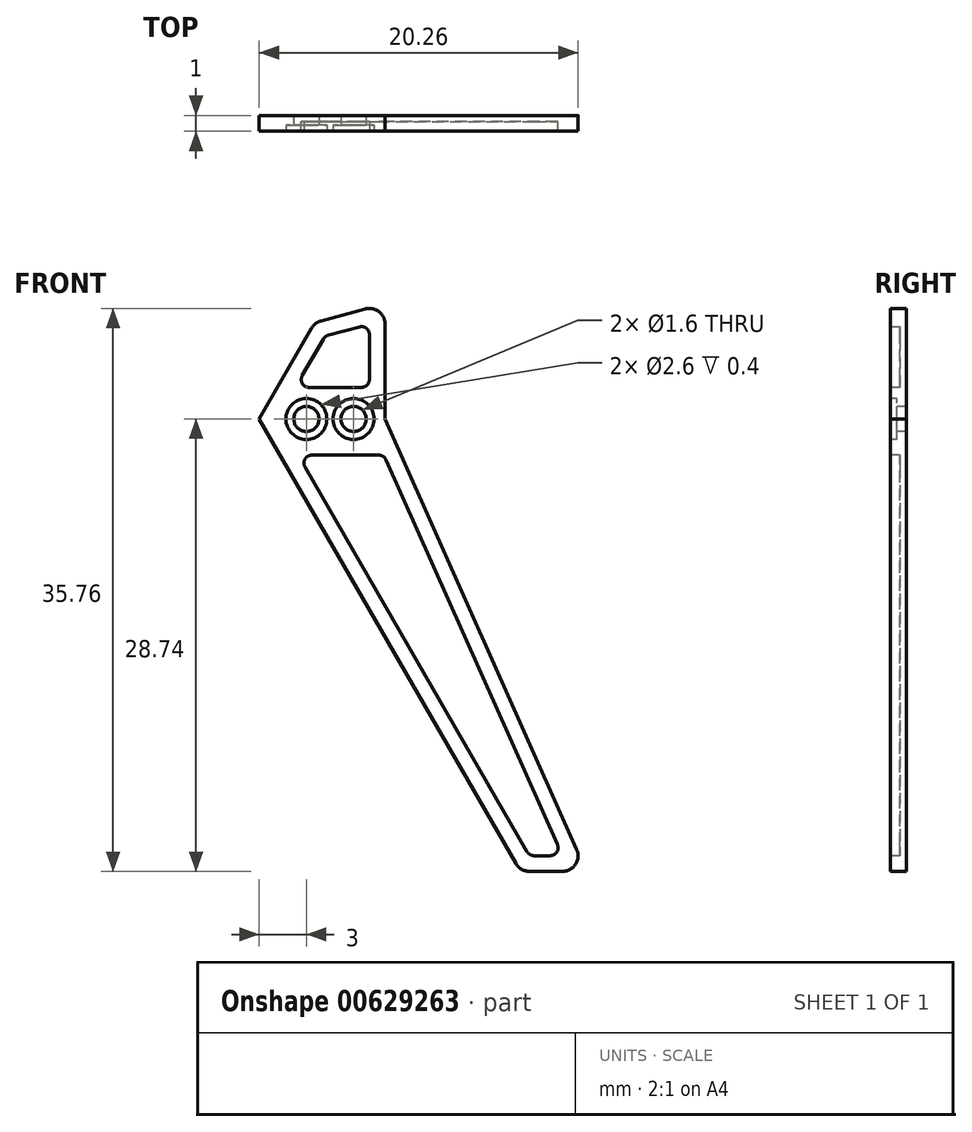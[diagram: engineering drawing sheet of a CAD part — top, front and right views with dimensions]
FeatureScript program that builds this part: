
annotation { "Feature Type Name" : "Feature", "Feature Type Description" : "" }
export const myFeature = defineFeature(function(context is Context, id is Id, definition is map)
    precondition{}
    {
        {
            var Q0;
            Q0=qCreatedBy(makeId("Front.planeOp"),FACE);
            var sketch = newSketch(context, id + "F0", { "sketchPlane" : qUnion([Q0])});
            skLineSegment(sketch, "E0", {"start": v(0, 0) * mm, "end": v(16.6, -28.74) * mm});
            skLineSegment(sketch, "E1", {"start": v(16.6, -28.74) * mm, "end": v(20.8, -28.74) * mm});
            skLineSegment(sketch, "E2", {"start": v(20.8, -28.74) * mm, "end": v(8, 0) * mm});
            skLineSegment(sketch, "E3", {"start": v(8, 0) * mm, "end": v(8, 7.32) * mm});
            skLineSegment(sketch, "E4", {"start": v(8, 7.32) * mm, "end": v(3.54, 6.12) * mm});
            skLineSegment(sketch, "E5", {"start": v(3.54, 6.12) * mm, "end": v(0, 0) * mm});
            skSolve(sketch);
        }
        {
            var Q0;
            Q0 = qSketchRegion(id + "F0", true);
            extrude(context, id + "F1", {"entities" : qUnion([Q0]), "depth" : 1 * mm, "offsetDistance" : 25 * mm});
        }
        {
            var Q0;
            Q0=makeQuery(id+"F1.opExtrude","CAP_FACE",FACE,{"disambiguationData":[OSD([sQuery(id+"F0.wireOp",EDGE,"E0"),sQuery(id+"F0.wireOp",EDGE,"E1"),sQuery(id+"F0.wireOp",EDGE,"E2"),sQuery(id+"F0.wireOp",EDGE,"E3"),sQuery(id+"F0.wireOp",EDGE,"E4"),sQuery(id+"F0.wireOp",EDGE,"E5")])],"isStart":false});
            var sketch = newSketch(context, id + "F2", { "sketchPlane" : qUnion([Q0])});
            skPoint(sketch, "E6", {"position": v(3, 0) * mm});
            skPoint(sketch, "E7", {"position": v(6, 0) * mm});
            skLineSegment(sketch, "E8", {"start": v(0, 0) * mm, "end": v(0, 6.46) * mm, "construction": true});
            skCircle(sketch, "E9", {"center": v(3, 0) * mm, "radius": 0.8 * mm});
            skCircle(sketch, "E10", {"center": v(6, 0) * mm, "radius": 0.8 * mm});
            skSolve(sketch);
        }
        {
            var Q0;
            Q0 = qSketchRegion(id + "F2", true);
            extrude(context, id + "F3", {"entities" : qUnion([Q0]), "operationType" : NewBodyOperationType.REMOVE, "oppositeDirection" : true, "depth" : 25 * mm, "offsetDistance" : 25 * mm, "hasSecondDirection" : true, "secondDirectionOppositeDirection" : false, "secondDirectionDepth" : 25 * mm});
        }
        {
            var Q0;
            Q0=makeQuery(id+"F1.opExtrude","CAP_FACE",FACE,{"disambiguationData":[OSD([sQuery(id+"F0.wireOp",EDGE,"E0"),sQuery(id+"F0.wireOp",EDGE,"E1"),sQuery(id+"F0.wireOp",EDGE,"E2"),sQuery(id+"F0.wireOp",EDGE,"E3"),sQuery(id+"F0.wireOp",EDGE,"E4"),sQuery(id+"F0.wireOp",EDGE,"E5")])],"isStart":false});
            var sketch = newSketch(context, id + "F4", { "sketchPlane" : qUnion([Q0])});
            skLineSegment(sketch, "E11", {"start": v(3.98, -3.53) * mm, "end": v(16.3, -26.24) * mm});
            skLineSegment(sketch, "E12", {"start": v(16.3, -26.24) * mm, "end": v(18.59, -26.24) * mm});
            skLineSegment(sketch, "E13", {"start": v(18.59, -26.24) * mm, "end": v(8, -3.53) * mm});
            skLineSegment(sketch, "E14", {"start": v(8, -3.53) * mm, "end": v(3.98, -3.53) * mm});
            skSolve(sketch);
        }
        {
            var Q0;
            Q0 = qSketchRegion(id + "F4", true);
            extrude(context, id + "F5", {"entities" : qUnion([Q0]), "operationType" : NewBodyOperationType.REMOVE, "endBound" : BoundingType.THROUGH_ALL, "oppositeDirection" : true, "depth" : 25 * mm, "offsetDistance" : 25 * mm, "hasSecondDirection" : true, "secondDirectionOppositeDirection" : true, "secondDirectionDepth" : 25 * mm});
        }
        {
            var Q0;
            Q0=makeQuery(id+"F1.opExtrude","SWEPT_EDGE",EDGE,{"disambiguationData":[OSD([sQuery(id+"F0.wireOp",EDGE,"E0"),sQuery(id+"F0.wireOp",EDGE,"E1")])]});
            var Q1;
            Q1=makeQuery(id+"F1.opExtrude","SWEPT_EDGE",EDGE,{"disambiguationData":[OSD([sQuery(id+"F0.wireOp",EDGE,"E1"),sQuery(id+"F0.wireOp",EDGE,"E2")])]});
            var Q2;
            Q2=makeQuery(id+"F1.opExtrude","SWEPT_EDGE",EDGE,{"disambiguationData":[OSD([sQuery(id+"F0.wireOp",EDGE,"E4"),sQuery(id+"F0.wireOp",EDGE,"E5")])]});
            var Q3;
            Q3=makeQuery(id+"F1.opExtrude","SWEPT_EDGE",EDGE,{"disambiguationData":[OSD([sQuery(id+"F0.wireOp",EDGE,"E3"),sQuery(id+"F0.wireOp",EDGE,"E4")])]});
            fillet(context, id + "F6", {"entities" : qUnion([Q0, Q1, Q2, Q3]), "radius" : 1 * mm, "tangentPropagation" : true, "allowEdgeOverflow" : false});
        }
        {
            var Q0;
            Q0=makeQuery(id+"F1.opExtrude","CAP_FACE",FACE,{"disambiguationData":[OSD([sQuery(id+"F0.wireOp",EDGE,"E0"),sQuery(id+"F0.wireOp",EDGE,"E1"),sQuery(id+"F0.wireOp",EDGE,"E2"),sQuery(id+"F0.wireOp",EDGE,"E3"),sQuery(id+"F0.wireOp",EDGE,"E4"),sQuery(id+"F0.wireOp",EDGE,"E5")])],"isStart":false});
            var sketch = newSketch(context, id + "F7", { "sketchPlane" : qUnion([Q0])});
            skLineSegment(sketch, "E15.0", {"start": v(7, 6.02) * mm, "end": v(7, 6.02) * mm});
            skLineSegment(sketch, "E15.1", {"start": v(7, 2) * mm, "end": v(7, 6.02) * mm});
            skLineSegment(sketch, "E15.2", {"start": v(7, 6.02) * mm, "end": v(4.2, 5.27) * mm});
            skLineSegment(sketch, "E15.3", {"start": v(19.26, -27.74) * mm, "end": v(7.93, -2.3) * mm});
            skLineSegment(sketch, "E15.4", {"start": v(19.26, -27.74) * mm, "end": v(19.26, -27.74) * mm});
            skLineSegment(sketch, "E15.5", {"start": v(17.17, -27.74) * mm, "end": v(19.26, -27.74) * mm});
            skLineSegment(sketch, "E15.6", {"start": v(4.2, 5.27) * mm, "end": v(4.2, 5.27) * mm});
            skLineSegment(sketch, "E15.7", {"start": v(4.2, 5.27) * mm, "end": v(2.3, 2) * mm});
            skLineSegment(sketch, "E15.8", {"start": v(2.48, -2.3) * mm, "end": v(17.17, -27.74) * mm});
            skLineSegment(sketch, "E15.9", {"start": v(17.17, -27.74) * mm, "end": v(17.17, -27.74) * mm});
            skLineSegment(sketch, "E16", {"start": v(2.3, 2) * mm, "end": v(7, 2) * mm});
            skLineSegment(sketch, "E17", {"start": v(2.48, -2.3) * mm, "end": v(7.93, -2.3) * mm});
            skSolve(sketch);
        }
        {
            var Q0;
            Q0 = qSketchRegion(id + "F7", true);
            extrude(context, id + "F8", {"entities" : qUnion([Q0]), "operationType" : NewBodyOperationType.REMOVE, "oppositeDirection" : true, "depth" : 0.6 * mm, "offsetDistance" : 25 * mm});
        }
        {
            var Q0;
            Q0=makeQuery(id+"F8.boolean.opBoolean","COPY",EDGE,{"derivedFrom":makeQuery(id+"F8.opExtrude","SWEPT_EDGE",EDGE,{"disambiguationData":[OSD([sQuery(id+"F7.wireOp",EDGE,"E15.7"),sQuery(id+"F7.wireOp",EDGE,"E16")])]})});
            var Q1;
            Q1=makeQuery(id+"F8.boolean.opBoolean","COPY",EDGE,{"derivedFrom":makeQuery(id+"F8.opExtrude","SWEPT_EDGE",EDGE,{"disambiguationData":[OSD([sQuery(id+"F7.wireOp",EDGE,"E15.1"),sQuery(id+"F7.wireOp",EDGE,"E16")])]})});
            var Q2;
            Q2=makeQuery(id+"F8.boolean.opBoolean","COPY",EDGE,{"derivedFrom":makeQuery(id+"F8.opExtrude","SWEPT_EDGE",EDGE,{"disambiguationData":[OSD([sQuery(id+"F7.wireOp",EDGE,"E15.1"),sQuery(id+"F7.wireOp",EDGE,"E15.2")])]})});
            var Q3;
            Q3=makeQuery(id+"F8.boolean.opBoolean","COPY",EDGE,{"derivedFrom":makeQuery(id+"F8.opExtrude","SWEPT_EDGE",EDGE,{"disambiguationData":[OSD([sQuery(id+"F7.wireOp",EDGE,"E15.2"),sQuery(id+"F7.wireOp",EDGE,"E15.7")])]})});
            var Q4;
            Q4=makeQuery(id+"F8.boolean.opBoolean","COPY",EDGE,{"derivedFrom":makeQuery(id+"F8.opExtrude","SWEPT_EDGE",EDGE,{"disambiguationData":[OSD([sQuery(id+"F7.wireOp",EDGE,"E15.3"),sQuery(id+"F7.wireOp",EDGE,"E17")])]})});
            var Q5;
            Q5=makeQuery(id+"F8.boolean.opBoolean","COPY",EDGE,{"derivedFrom":makeQuery(id+"F8.opExtrude","SWEPT_EDGE",EDGE,{"disambiguationData":[OSD([sQuery(id+"F7.wireOp",EDGE,"E15.8"),sQuery(id+"F7.wireOp",EDGE,"E17")])]})});
            var Q6;
            Q6=makeQuery(id+"F8.boolean.opBoolean","COPY",EDGE,{"derivedFrom":makeQuery(id+"F8.opExtrude","SWEPT_EDGE",EDGE,{"disambiguationData":[OSD([sQuery(id+"F7.wireOp",EDGE,"E15.3"),sQuery(id+"F7.wireOp",EDGE,"E15.5")])]})});
            var Q7;
            Q7=makeQuery(id+"F8.boolean.opBoolean","COPY",EDGE,{"derivedFrom":makeQuery(id+"F8.opExtrude","SWEPT_EDGE",EDGE,{"disambiguationData":[OSD([sQuery(id+"F7.wireOp",EDGE,"E15.5"),sQuery(id+"F7.wireOp",EDGE,"E15.8")])]})});
            fillet(context, id + "F9", {"entities" : qUnion([Q0, Q1, Q2, Q3, Q4, Q5, Q6, Q7]), "radius" : 0.5 * mm, "tangentPropagation" : true, "allowEdgeOverflow" : false});
        }
        {
            var Q0;
            Q0=makeQuery(id+"F1.opExtrude","CAP_FACE",FACE,{"disambiguationData":[OSD([sQuery(id+"F0.wireOp",EDGE,"E0"),sQuery(id+"F0.wireOp",EDGE,"E1"),sQuery(id+"F0.wireOp",EDGE,"E2"),sQuery(id+"F0.wireOp",EDGE,"E3"),sQuery(id+"F0.wireOp",EDGE,"E4"),sQuery(id+"F0.wireOp",EDGE,"E5")])],"isStart":false});
            var sketch = newSketch(context, id + "F10", { "sketchPlane" : qUnion([Q0])});
            skCircle(sketch, "E18", {"center": v(3, 0) * mm, "radius": 1.3 * mm});
            skCircle(sketch, "E19", {"center": v(6, 0) * mm, "radius": 1.3 * mm});
            skSolve(sketch);
        }
        {
            var Q0;
            Q0 = qSketchRegion(id + "F10", true);
            extrude(context, id + "F11", {"entities" : qUnion([Q0]), "operationType" : NewBodyOperationType.REMOVE, "oppositeDirection" : true, "depth" : 0.4 * mm, "offsetDistance" : 25 * mm});
        }
    });
